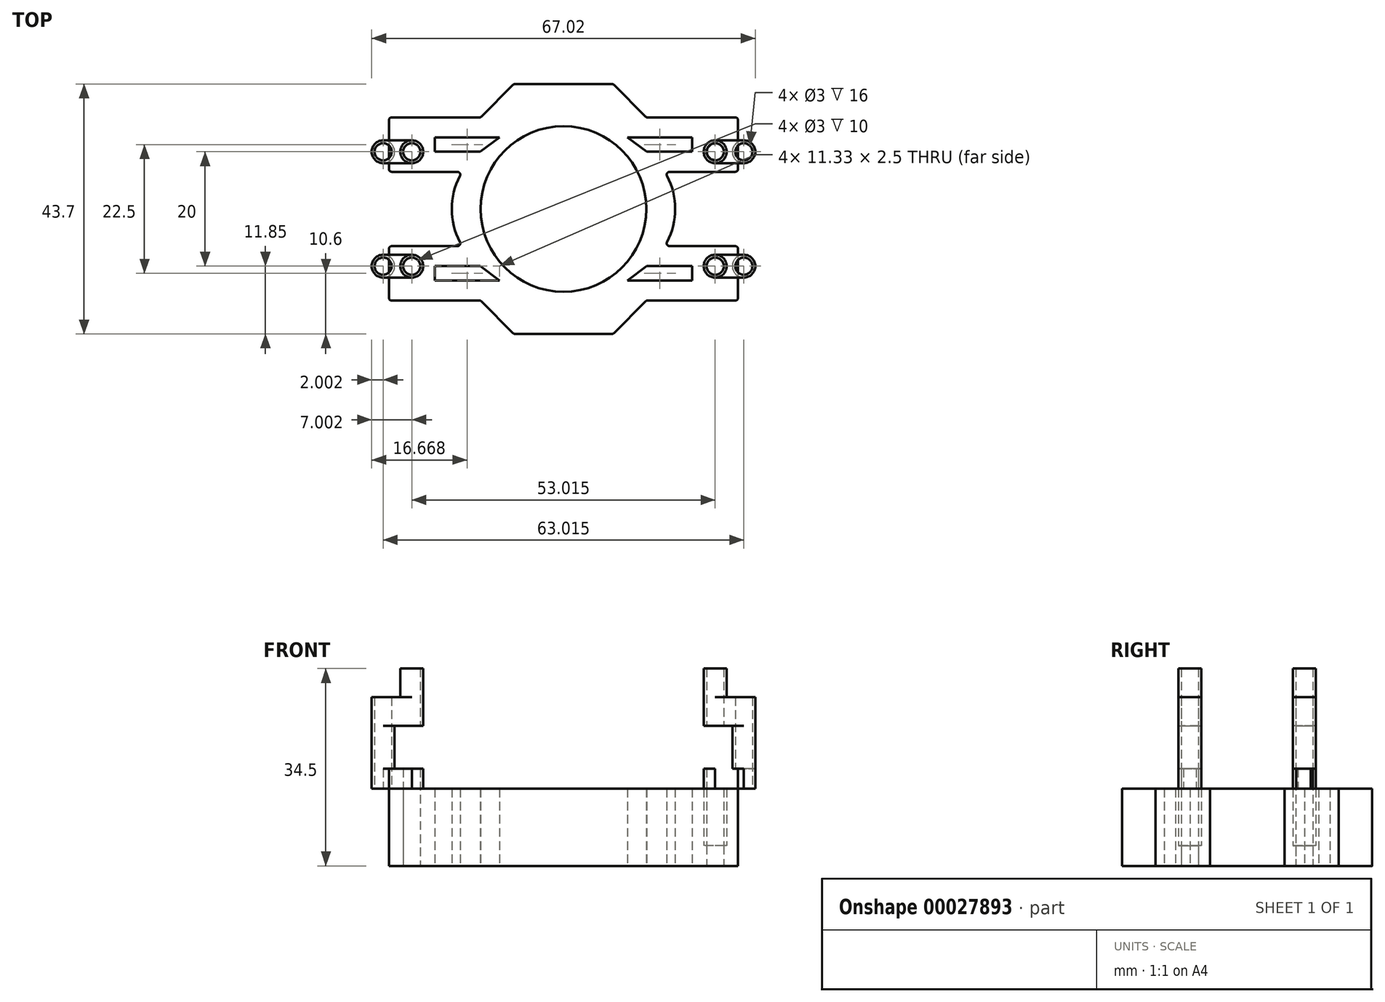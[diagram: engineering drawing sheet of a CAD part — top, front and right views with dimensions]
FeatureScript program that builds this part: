
annotation { "Feature Type Name" : "Feature", "Feature Type Description" : "" }
export const myFeature = defineFeature(function(context is Context, id is Id, definition is map)
    precondition{}
    {
        {
            var Q0;
            Q0=qCreatedBy(makeId("Top.planeOp"),FACE);
            var sketch = newSketch(context, id + "F0", { "sketchPlane" : qUnion([Q0])});
            skLineSegment(sketch, "E0.rect.bottom", {"start": v(30.5, 16) * mm, "end": v(-30.5, 16) * mm});
            skLineSegment(sketch, "E0.rect.top", {"start": v(30.5, -16) * mm, "end": v(-30.5, -16) * mm});
            skLineSegment(sketch, "E0.rect.left", {"start": v(30.5, 16) * mm, "end": v(30.5, -16) * mm});
            skLineSegment(sketch, "E0.rect.right", {"start": v(-30.5, 16) * mm, "end": v(-30.5, -16) * mm});
            skPoint(sketch, "E0.rect.middle", {"position": v(0, 0) * mm});
            skCircle(sketch, "E1", {"center": v(0, 0) * mm, "radius": 14.47 * mm});
            skLineSegment(sketch, "E2.rect.bottom", {"start": v(-19.5, -10) * mm, "end": v(-22.5, -10) * mm});
            skLineSegment(sketch, "E2.rect.top", {"start": v(-19.5, 10) * mm, "end": v(-22.5, 10) * mm});
            skLineSegment(sketch, "E2.rect.left", {"start": v(-19.5, -10) * mm, "end": v(-19.5, 10) * mm});
            skLineSegment(sketch, "E2.rect.right", {"start": v(-22.5, -10) * mm, "end": v(-22.5, 10) * mm});
            skPoint(sketch, "E2.rect.middle", {"position": v(-21, 0) * mm});
            skLineSegment(sketch, "E3.MirrorCS", {"start": v(19.5, 10) * mm, "end": v(22.5, 10) * mm});
            skLineSegment(sketch, "E4.MirrorCS", {"start": v(22.5, -10) * mm, "end": v(22.5, 10) * mm});
            skLineSegment(sketch, "E5.MirrorCS", {"start": v(19.5, -10) * mm, "end": v(22.5, -10) * mm});
            skLineSegment(sketch, "E6.MirrorCS", {"start": v(19.5, -10) * mm, "end": v(19.5, 10) * mm});
            skCircle(sketch, "E7", {"center": v(-26.5, 10) * mm, "radius": 1.5 * mm});
            skCircle(sketch, "E8", {"center": v(-26.5, -10) * mm, "radius": 1.5 * mm});
            skCircle(sketch, "E9.MirrorC", {"center": v(26.5, 10) * mm, "radius": 1.5 * mm});
            skCircle(sketch, "E10.MirrorC", {"center": v(26.5, -10) * mm, "radius": 1.5 * mm});
            skLineSegment(sketch, "E11", {"start": v(-19.5, -10) * mm, "end": v(-14.5, -10) * mm});
            skLineSegment(sketch, "E12", {"start": v(-19.5, 10) * mm, "end": v(-14.5, 10) * mm});
            skArc(sketch, "E13", {"start": v(-14.5, 10) * mm, "mid": v(-19.5, 0) * mm, "end": v(-14.5, -10) * mm});
            skArc(sketch, "E14.MirrorCS", {"start": v(14.5, 10) * mm, "mid": v(19.5, 0) * mm, "end": v(14.5, -10) * mm});
            skLineSegment(sketch, "E15.MirrorCS", {"start": v(19.5, -10) * mm, "end": v(14.5, -10) * mm});
            skLineSegment(sketch, "E16.MirrorCS", {"start": v(19.5, 10) * mm, "end": v(14.5, 10) * mm});
            skLineSegment(sketch, "E17", {"start": v(-22.5, 6.5) * mm, "end": v(-19.5, 6.5) * mm});
            skLineSegment(sketch, "E18", {"start": v(-22.5, -6.5) * mm, "end": v(-19.5, -6.5) * mm});
            skLineSegment(sketch, "E19", {"start": v(-19.5, -6.5) * mm, "end": v(-17.69, -6.5) * mm});
            skLineSegment(sketch, "E20", {"start": v(-19.5, 6.5) * mm, "end": v(-17.69, 6.5) * mm});
            skLineSegment(sketch, "E21.bottom", {"start": v(-22.5, 6.5) * mm, "end": v(-30.5, 6.5) * mm});
            skLineSegment(sketch, "E21.top", {"start": v(-22.5, -6.5) * mm, "end": v(-30.5, -6.5) * mm});
            skLineSegment(sketch, "E21.left", {"start": v(-22.5, 6.5) * mm, "end": v(-22.5, -6.5) * mm});
            skLineSegment(sketch, "E21.right", {"start": v(-30.5, 6.5) * mm, "end": v(-30.5, -6.5) * mm});
            skLineSegment(sketch, "E22.MirrorCS", {"start": v(19.5, 6.5) * mm, "end": v(17.69, 6.5) * mm});
            skLineSegment(sketch, "E23.MirrorCS", {"start": v(22.5, 6.5) * mm, "end": v(19.5, 6.5) * mm});
            skLineSegment(sketch, "E24.MirrorCS", {"start": v(22.5, 6.5) * mm, "end": v(30.5, 6.5) * mm});
            skLineSegment(sketch, "E25.MirrorCS", {"start": v(22.5, -6.5) * mm, "end": v(30.5, -6.5) * mm});
            skLineSegment(sketch, "E26.MirrorCS", {"start": v(22.5, -6.5) * mm, "end": v(19.5, -6.5) * mm});
            skLineSegment(sketch, "E27.MirrorCS", {"start": v(19.5, -6.5) * mm, "end": v(17.69, -6.5) * mm});
            skLineSegment(sketch, "E28", {"start": v(-14.5, -16) * mm, "end": v(-8.66, -21.85) * mm});
            skLineSegment(sketch, "E29", {"start": v(-8.66, -21.85) * mm, "end": v(8.66, -21.85) * mm});
            skLineSegment(sketch, "E30", {"start": v(8.66, -21.85) * mm, "end": v(14.5, -16) * mm});
            skLineSegment(sketch, "E31.MirrorCS", {"start": v(-8.66, -21.85) * mm, "end": v(-8.66, -39.17) * mm});
            skLineSegment(sketch, "E32.MirrorCS", {"start": v(-14.5, 16) * mm, "end": v(-8.66, 21.85) * mm});
            skLineSegment(sketch, "E33.MirrorCS", {"start": v(-8.66, 21.85) * mm, "end": v(8.66, 21.85) * mm});
            skLineSegment(sketch, "E34.MirrorCS", {"start": v(8.66, 21.85) * mm, "end": v(14.5, 16) * mm});
            skLineSegment(sketch, "E35.bottom", {"start": v(-14.5, -10) * mm, "end": v(-22.5, -10) * mm});
            skLineSegment(sketch, "E35.top", {"start": v(-14.5, -12.5) * mm, "end": v(-22.5, -12.5) * mm});
            skLineSegment(sketch, "E35.left", {"start": v(-14.5, -10) * mm, "end": v(-14.5, -12.5) * mm});
            skLineSegment(sketch, "E35.right", {"start": v(-22.5, -10) * mm, "end": v(-22.5, -12.5) * mm});
            skLineSegment(sketch, "E36", {"start": v(30.5, 0) * mm, "end": v(-30.5, 0) * mm, "construction": true});
            skLineSegment(sketch, "E37", {"start": v(0, -21.85) * mm, "end": v(0, 21.85) * mm, "construction": true});
            skLineSegment(sketch, "E38.MirrorCS", {"start": v(-14.5, 12.5) * mm, "end": v(-22.5, 12.5) * mm});
            skLineSegment(sketch, "E39.MirrorCS", {"start": v(-22.5, 10) * mm, "end": v(-22.5, 12.5) * mm});
            skLineSegment(sketch, "E40.MirrorCS", {"start": v(-14.5, 10) * mm, "end": v(-14.5, 12.5) * mm});
            skLineSegment(sketch, "E41.MirrorCS", {"start": v(-45.02, -21.85) * mm, "end": v(-45.02, 21.85) * mm});
            skLineSegment(sketch, "E42.MirrorCS", {"start": v(14.5, 10) * mm, "end": v(14.5, 12.5) * mm});
            skLineSegment(sketch, "E43.MirrorCS", {"start": v(14.5, 12.5) * mm, "end": v(22.5, 12.5) * mm});
            skLineSegment(sketch, "E44.MirrorCS", {"start": v(22.5, 10) * mm, "end": v(22.5, 12.5) * mm});
            skLineSegment(sketch, "E45.MirrorCS", {"start": v(22.5, -10) * mm, "end": v(22.5, -12.5) * mm});
            skLineSegment(sketch, "E46.MirrorCS", {"start": v(14.5, -12.5) * mm, "end": v(22.5, -12.5) * mm});
            skLineSegment(sketch, "E47.MirrorCS", {"start": v(14.5, -10) * mm, "end": v(14.5, -12.5) * mm});
            skLineSegment(sketch, "E48", {"start": v(-14.5, -12.5) * mm, "end": v(-12, -12.5) * mm});
            skLineSegment(sketch, "E49", {"start": v(-14.5, -10) * mm, "end": v(-11.18, -12.5) * mm});
            skLineSegment(sketch, "E50", {"start": v(-11.18, -12.5) * mm, "end": v(-12, -12.5) * mm});
            skLineSegment(sketch, "E51.MirrorCS", {"start": v(14.5, -12.5) * mm, "end": v(12, -12.5) * mm});
            skLineSegment(sketch, "E52.MirrorCS", {"start": v(11.18, -12.5) * mm, "end": v(12, -12.5) * mm});
            skLineSegment(sketch, "E53.MirrorCS", {"start": v(14.5, -10) * mm, "end": v(11.18, -12.5) * mm});
            skLineSegment(sketch, "E54.MirrorCS", {"start": v(14.5, 12.5) * mm, "end": v(12, 12.5) * mm});
            skLineSegment(sketch, "E55.MirrorCS", {"start": v(11.18, 12.5) * mm, "end": v(12, 12.5) * mm});
            skLineSegment(sketch, "E56.MirrorCS", {"start": v(14.5, 10) * mm, "end": v(11.18, 12.5) * mm});
            skLineSegment(sketch, "E57.MirrorCS", {"start": v(-14.5, 12.5) * mm, "end": v(-12, 12.5) * mm});
            skLineSegment(sketch, "E58.MirrorCS", {"start": v(-11.18, 12.5) * mm, "end": v(-12, 12.5) * mm});
            skLineSegment(sketch, "E59.MirrorCS", {"start": v(-14.5, 10) * mm, "end": v(-11.18, 12.5) * mm});
            skSolve(sketch);
        }
        {
            var Q0;
            Q0=makeQuery(id+"F0.imprint","IMPRINT",FACE,{"disambiguationData":[TD([[makeQuery(id+"F0.imprint","IMPRINT",EDGE,{"derivedFrom":sQuery(id+"F0.wireOp",EDGE,"E0.rect.bottom")}),1.0]])]});
            var Q1;
            {var subQ2=sQuery(id+"F0.wireOp",EDGE,"E2.rect.top");Q1=makeQuery(id+"F0.imprint","IMPRINT",FACE,{"disambiguationData":[TD([[makeQuery(id+"F0.imprint","IMPRINT",EDGE,{"derivedFrom":subQ2}),1.0]])]});}
            var Q2;
            {var subQ2=sQuery(id+"F0.wireOp",EDGE,"E12");Q2=makeQuery(id+"F0.imprint","IMPRINT",FACE,{"disambiguationData":[TD([[makeQuery(id+"F0.imprint","IMPRINT",EDGE,{"derivedFrom":subQ2}),-1.0]])]});}
            var Q3;
            {var subQ2=sQuery(id+"F0.wireOp",EDGE,"E2.rect.bottom");Q3=makeQuery(id+"F0.imprint","IMPRINT",FACE,{"disambiguationData":[TD([[makeQuery(id+"F0.imprint","IMPRINT",EDGE,{"derivedFrom":subQ2}),-1.0]])]});}
            var Q4;
            {var subQ2=sQuery(id+"F0.wireOp",EDGE,"E11");Q4=makeQuery(id+"F0.imprint","IMPRINT",FACE,{"disambiguationData":[TD([[makeQuery(id+"F0.imprint","IMPRINT",EDGE,{"derivedFrom":subQ2}),1.0]])]});}
            var Q5;
            {var subQ2=sQuery(id+"F0.wireOp",EDGE,"E16.MirrorCS");Q5=makeQuery(id+"F0.imprint","IMPRINT",FACE,{"disambiguationData":[TD([[makeQuery(id+"F0.imprint","IMPRINT",EDGE,{"derivedFrom":subQ2}),1.0]])]});}
            var Q6;
            {var subQ2=sQuery(id+"F0.wireOp",EDGE,"E3.MirrorCS");Q6=makeQuery(id+"F0.imprint","IMPRINT",FACE,{"disambiguationData":[TD([[makeQuery(id+"F0.imprint","IMPRINT",EDGE,{"derivedFrom":subQ2}),-1.0]])]});}
            var Q7;
            {var subQ1=sQuery(id+"F0.wireOp",EDGE,"E15.MirrorCS");Q7=makeQuery(id+"F0.imprint","IMPRINT",FACE,{"disambiguationData":[TD([[makeQuery(id+"F0.imprint","IMPRINT",EDGE,{"derivedFrom":subQ1}),-1.0]])]});}
            var Q8;
            {var subQ2=sQuery(id+"F0.wireOp",EDGE,"E5.MirrorCS");Q8=makeQuery(id+"F0.imprint","IMPRINT",FACE,{"disambiguationData":[TD([[makeQuery(id+"F0.imprint","IMPRINT",EDGE,{"derivedFrom":subQ2}),1.0]])]});}
            var Q9;
            {var subQ1=sQuery(id+"F0.wireOp",EDGE,"E28");Q9=makeQuery(id+"F0.imprint","IMPRINT",FACE,{"disambiguationData":[TD([[makeQuery(id+"F0.imprint","IMPRINT",EDGE,{"derivedFrom":subQ1}),1.0]])]});}
            var Q10;
            {var subQ1=sQuery(id+"F0.wireOp",EDGE,"E32.MirrorCS");Q10=makeQuery(id+"F0.imprint","IMPRINT",FACE,{"disambiguationData":[TD([[makeQuery(id+"F0.imprint","IMPRINT",EDGE,{"derivedFrom":subQ1}),-1.0]])]});}
            var Q11;
            {var subQ5=sQuery(id+"F0.wireOp",EDGE,"E18");Q11=makeQuery(id+"F0.imprint","IMPRINT",FACE,{"disambiguationData":[TD([[makeQuery(id+"F0.imprint","IMPRINT",EDGE,{"derivedFrom":subQ5}),-1.0]])]});}
            var Q12;
            {var subQ5=sQuery(id+"F0.wireOp",EDGE,"E19");Q12=makeQuery(id+"F0.imprint","IMPRINT",FACE,{"disambiguationData":[TD([[makeQuery(id+"F0.imprint","IMPRINT",EDGE,{"derivedFrom":subQ5}),-1.0]])]});}
            extrude(context, id + "F1", {"entities" : qUnion([Q0, Q1, Q2, Q3, Q4, Q5, Q6, Q7, Q8, Q9, Q10, Q11, Q12]), "depth" : 3.5 * mm});
        }
        {
            var Q0;
            Q0=makeQuery(id+"F1.opExtrude","CAP_FACE",FACE,{"disambiguationData":[OSD([sQuery(id+"F0.wireOp",EDGE,"E0.rect.bottom"),sQuery(id+"F0.wireOp",EDGE,"E0.rect.top"),sQuery(id+"F0.wireOp",EDGE,"E0.rect.left"),sQuery(id+"F0.wireOp",EDGE,"E0.rect.right"),sQuery(id+"F0.wireOp",EDGE,"E1"),sQuery(id+"F0.wireOp",EDGE,"E7"),sQuery(id+"F0.wireOp",EDGE,"E8"),sQuery(id+"F0.wireOp",EDGE,"E9.MirrorC"),sQuery(id+"F0.wireOp",EDGE,"E10.MirrorC"),sQuery(id+"F0.wireOp",EDGE,"E13"),sQuery(id+"F0.wireOp",EDGE,"E14.MirrorCS"),sQuery(id+"F0.wireOp",EDGE,"E17"),sQuery(id+"F0.wireOp",EDGE,"E18"),sQuery(id+"F0.wireOp",EDGE,"E19"),sQuery(id+"F0.wireOp",EDGE,"E21.bottom"),sQuery(id+"F0.wireOp",EDGE,"E21.top"),sQuery(id+"F0.wireOp",EDGE,"E20"),sQuery(id+"F0.wireOp",EDGE,"E22.MirrorCS"),sQuery(id+"F0.wireOp",EDGE,"E23.MirrorCS"),sQuery(id+"F0.wireOp",EDGE,"E24.MirrorCS"),sQuery(id+"F0.wireOp",EDGE,"E25.MirrorCS"),sQuery(id+"F0.wireOp",EDGE,"E26.MirrorCS"),sQuery(id+"F0.wireOp",EDGE,"E27.MirrorCS")])],"isStart":false});
            var sketch = newSketch(context, id + "F2", { "sketchPlane" : qUnion([Q0])});
            skCircle(sketch, "E60", {"center": v(-26.5, 10) * mm, "radius": 1.5 * mm});
            skCircle(sketch, "E61", {"center": v(-26.5, 10) * mm, "radius": 2 * mm});
            skCircle(sketch, "E62.MirrorC", {"center": v(26.5, 10) * mm, "radius": 2 * mm});
            skCircle(sketch, "E63.MirrorC", {"center": v(26.5, 10) * mm, "radius": 1.5 * mm});
            skCircle(sketch, "E64.MirrorC", {"center": v(-26.5, -10) * mm, "radius": 1.5 * mm});
            skCircle(sketch, "E65.MirrorC", {"center": v(-26.5, -10) * mm, "radius": 2 * mm});
            skCircle(sketch, "E66.MirrorC", {"center": v(26.5, -10) * mm, "radius": 1.5 * mm});
            skCircle(sketch, "E67.MirrorC", {"center": v(26.5, -10) * mm, "radius": 2 * mm});
            skSolve(sketch);
        }
        {
            var Q0;
            Q0=makeQuery(id+"F2.imprint","IMPRINT",FACE,{"disambiguationData":[TD([[makeQuery(id+"F2.imprint","IMPRINT",EDGE,{"derivedFrom":sQuery(id+"F2.wireOp",EDGE,"E60")}),-1.0]])]});
            var Q1;
            Q1=makeQuery(id+"F2.imprint","IMPRINT",FACE,{"disambiguationData":[TD([[makeQuery(id+"F2.imprint","IMPRINT",EDGE,{"derivedFrom":sQuery(id+"F2.wireOp",EDGE,"E64.MirrorC")}),-1.0]])]});
            var Q2;
            Q2=makeQuery(id+"F2.imprint","IMPRINT",FACE,{"disambiguationData":[TD([[makeQuery(id+"F2.imprint","IMPRINT",EDGE,{"derivedFrom":sQuery(id+"F2.wireOp",EDGE,"E66.MirrorC")}),1.0]])]});
            var Q3;
            Q3=makeQuery(id+"F2.imprint","IMPRINT",FACE,{"disambiguationData":[TD([[makeQuery(id+"F2.imprint","IMPRINT",EDGE,{"derivedFrom":sQuery(id+"F2.wireOp",EDGE,"E62.MirrorC")}),-1.0]])]});
            extrude(context, id + "F3", {"entities" : qUnion([Q0, Q1, Q2, Q3]), "operationType" : NewBodyOperationType.ADD, "depth" : 10 * mm});
        }
        {
            var Q0;
            Q0=makeQuery(id+"F1.opExtrude","SWEPT_EDGE",EDGE,{"disambiguationData":[OSD([sQuery(id+"F0.wireOp",EDGE,"E14.MirrorCS"),sQuery(id+"F0.wireOp",EDGE,"E22.MirrorCS")])]});
            var Q1;
            Q1=makeQuery(id+"F1.opExtrude","SWEPT_EDGE",EDGE,{"disambiguationData":[OSD([sQuery(id+"F0.wireOp",EDGE,"E14.MirrorCS"),sQuery(id+"F0.wireOp",EDGE,"E27.MirrorCS")])]});
            var Q2;
            Q2=makeQuery(id+"F1.opExtrude","SWEPT_EDGE",EDGE,{"disambiguationData":[OSD([sQuery(id+"F0.wireOp",EDGE,"E13"),sQuery(id+"F0.wireOp",EDGE,"E20")])]});
            var Q3;
            Q3=makeQuery(id+"F1.opExtrude","SWEPT_EDGE",EDGE,{"disambiguationData":[OSD([sQuery(id+"F0.wireOp",EDGE,"E13"),sQuery(id+"F0.wireOp",EDGE,"E19")])]});
            var Q4;
            Q4=makeQuery(id+"F1.opExtrude","SWEPT_EDGE",EDGE,{"disambiguationData":[OSD([sQuery(id+"F0.wireOp",EDGE,"E0.rect.top"),sQuery(id+"F0.wireOp",EDGE,"E0.rect.right")])]});
            var Q5;
            Q5=makeQuery(id+"F1.opExtrude","SWEPT_EDGE",EDGE,{"disambiguationData":[OSD([sQuery(id+"F0.wireOp",EDGE,"E0.rect.top"),sQuery(id+"F0.wireOp",EDGE,"E0.rect.left")])]});
            var Q6;
            Q6=makeQuery(id+"F1.opExtrude","SWEPT_EDGE",EDGE,{"disambiguationData":[OSD([sQuery(id+"F0.wireOp",EDGE,"E0.rect.left"),sQuery(id+"F0.wireOp",EDGE,"E25.MirrorCS")])]});
            var Q7;
            Q7=makeQuery(id+"F1.opExtrude","SWEPT_EDGE",EDGE,{"disambiguationData":[OSD([sQuery(id+"F0.wireOp",EDGE,"E0.rect.bottom"),sQuery(id+"F0.wireOp",EDGE,"E0.rect.left")])]});
            var Q8;
            Q8=makeQuery(id+"F1.opExtrude","SWEPT_EDGE",EDGE,{"disambiguationData":[OSD([sQuery(id+"F0.wireOp",EDGE,"E0.rect.left"),sQuery(id+"F0.wireOp",EDGE,"E24.MirrorCS")])]});
            var Q9;
            Q9=makeQuery(id+"F1.opExtrude","SWEPT_EDGE",EDGE,{"disambiguationData":[OSD([sQuery(id+"F0.wireOp",EDGE,"E0.rect.right"),sQuery(id+"F0.wireOp",EDGE,"E21.bottom"),sQuery(id+"F0.wireOp",EDGE,"E21.right")])]});
            var Q10;
            Q10=makeQuery(id+"F1.opExtrude","SWEPT_EDGE",EDGE,{"disambiguationData":[OSD([sQuery(id+"F0.wireOp",EDGE,"E0.rect.bottom"),sQuery(id+"F0.wireOp",EDGE,"E0.rect.right")])]});
            var Q11;
            Q11=makeQuery(id+"F1.opExtrude","SWEPT_EDGE",EDGE,{"disambiguationData":[OSD([sQuery(id+"F0.wireOp",EDGE,"E0.rect.right"),sQuery(id+"F0.wireOp",EDGE,"E21.top"),sQuery(id+"F0.wireOp",EDGE,"E21.right")])]});
            fillet(context, id + "F4", {"entities" : qUnion([Q0, Q1, Q2, Q3, Q4, Q5, Q6, Q7, Q8, Q9, Q10, Q11]), "radius" : .5 * mm, "tangentPropagation" : true, "allowEdgeOverflow" : false});
        }
        {
            var Q0;
            Q0=makeQuery(id+"F3.opExtrude","CAP_FACE",FACE,{"disambiguationData":[OSD([sQuery(id+"F2.wireOp",EDGE,"E60"),sQuery(id+"F2.wireOp",EDGE,"E61")])],"isStart":false});
            var sketch = newSketch(context, id + "F5", { "sketchPlane" : qUnion([Q0])});
            skLineSegment(sketch, "E68", {"start": v(-26.5, 12) * mm, "end": v(-26.5, 8) * mm, "construction": true});
            skLineSegment(sketch, "E69.bottom", {"start": v(-26.5, 12) * mm, "end": v(-31.5, 12) * mm});
            skLineSegment(sketch, "E69.top", {"start": v(-26.5, 8) * mm, "end": v(-31.5, 8) * mm});
            skLineSegment(sketch, "E69.right", {"start": v(-31.5, 12) * mm, "end": v(-31.5, 8) * mm});
            skArc(sketch, "E70", {"start": v(-31.5, 12) * mm, "mid": v(-33.5, 10) * mm, "end": v(-31.5, 8) * mm});
            skCircle(sketch, "E71", {"center": v(-31.5, 10) * mm, "radius": 1.5 * mm});
            skLineSegment(sketch, "E72", {"start": v(0, 59.27) * mm, "end": v(0, -61.45) * mm, "construction": true});
            skLineSegment(sketch, "E73", {"start": v(-74.65, 0) * mm, "end": v(75.38, 0) * mm, "construction": true});
            skLineSegment(sketch, "E74.MirrorCS", {"start": v(26.5, 12) * mm, "end": v(31.5, 12) * mm});
            skLineSegment(sketch, "E75.MirrorCS", {"start": v(26.5, 12) * mm, "end": v(26.5, 8) * mm});
            skLineSegment(sketch, "E76.MirrorCS", {"start": v(26.5, 8) * mm, "end": v(31.5, 8) * mm});
            skArc(sketch, "E77.MirrorCS", {"start": v(31.5, 12) * mm, "mid": v(33.5, 10) * mm, "end": v(31.5, 8) * mm});
            skCircle(sketch, "E78.MirrorC", {"center": v(31.5, 10) * mm, "radius": 1.5 * mm});
            skLineSegment(sketch, "E79.MirrorCS", {"start": v(31.5, 12) * mm, "end": v(31.5, 8) * mm});
            skLineSegment(sketch, "E80.MirrorCS", {"start": v(-26.5, -8) * mm, "end": v(-31.5, -8) * mm});
            skLineSegment(sketch, "E81.MirrorCS", {"start": v(-26.5, -12) * mm, "end": v(-26.5, -8) * mm});
            skLineSegment(sketch, "E82.MirrorCS", {"start": v(-26.5, -12) * mm, "end": v(-31.5, -12) * mm});
            skArc(sketch, "E83.MirrorCS", {"start": v(-31.5, -12) * mm, "mid": v(-33.5, -10) * mm, "end": v(-31.5, -8) * mm});
            skLineSegment(sketch, "E84.MirrorCS", {"start": v(-31.5, -12) * mm, "end": v(-31.5, -8) * mm, "construction": true});
            skCircle(sketch, "E85.MirrorC", {"center": v(-31.5, -10) * mm, "radius": 1.5 * mm});
            skLineSegment(sketch, "E86.MirrorCS", {"start": v(-26.5, 12) * mm, "end": v(-26.5, 8) * mm});
            skLineSegment(sketch, "E87.MirrorCS", {"start": v(26.5, -8) * mm, "end": v(31.5, -8) * mm});
            skLineSegment(sketch, "E88.MirrorCS", {"start": v(26.5, -12) * mm, "end": v(26.5, -8) * mm});
            skLineSegment(sketch, "E89.MirrorCS", {"start": v(26.5, -12) * mm, "end": v(31.5, -12) * mm});
            skLineSegment(sketch, "E90.MirrorCS", {"start": v(31.5, -12) * mm, "end": v(31.5, -8) * mm});
            skCircle(sketch, "E91.MirrorC", {"center": v(31.5, -10) * mm, "radius": 1.5 * mm});
            skArc(sketch, "E92.MirrorCS", {"start": v(31.5, -12) * mm, "mid": v(33.5, -10) * mm, "end": v(31.5, -8) * mm});
            skArc(sketch, "E93", {"start": v(-26.5, 8) * mm, "mid": v(-24.5, 10) * mm, "end": v(-26.5, 12) * mm});
            skArc(sketch, "E94.MirrorCS", {"start": v(-26.5, -8) * mm, "mid": v(-24.5, -10) * mm, "end": v(-26.5, -12) * mm});
            skArc(sketch, "E95.MirrorCS", {"start": v(26.5, -8) * mm, "mid": v(24.5, -10) * mm, "end": v(26.5, -12) * mm});
            skArc(sketch, "E96.MirrorCS", {"start": v(26.5, 8) * mm, "mid": v(24.5, 10) * mm, "end": v(26.5, 12) * mm});
            skArc(sketch, "E97.MirrorCS", {"start": v(26.5, 8) * mm, "mid": v(28.5, 10) * mm, "end": v(26.5, 12) * mm});
            skCircle(sketch, "E98", {"center": v(26.5, 10) * mm, "radius": 1.46 * mm});
            skCircle(sketch, "E99", {"center": v(26.5, -10) * mm, "radius": 1.5 * mm});
            skCircle(sketch, "E100", {"center": v(-26.5, -10) * mm, "radius": 1.5 * mm});
            skSolve(sketch);
        }
        {
            var Q0;
            Q0=makeQuery(id+"F5.imprint","IMPRINT",FACE,{"disambiguationData":[TD([[makeQuery(id+"F5.imprint","IMPRINT",EDGE,{"derivedFrom":sQuery(id+"F5.wireOp",EDGE,"E75.MirrorCS")}),-1.0]])]});
            var Q1;
            Q1=makeQuery(id+"F5.imprint","IMPRINT",FACE,{"disambiguationData":[TD([[makeQuery(id+"F5.imprint","IMPRINT",EDGE,{"derivedFrom":sQuery(id+"F5.wireOp",EDGE,"E81.MirrorCS")}),-1.0]])]});
            var Q2;
            Q2=makeQuery(id+"F5.imprint","IMPRINT",FACE,{"disambiguationData":[TD([[makeQuery(id+"F5.imprint","IMPRINT",EDGE,{"derivedFrom":sQuery(id+"F5.wireOp",EDGE,"E88.MirrorCS")}),1.0]])]});
            var Q3;
            {var subQ0=sQuery(id+"F5.wireOp",EDGE,"E70");Q3=makeQuery(id+"F5.imprint","IMPRINT",FACE,{"disambiguationData":[TD([[makeQuery(id+"F5.imprint","IMPRINT",EDGE,{"derivedFrom":subQ0}),1.0]])]});}
            var Q4;
            {var subQ3=sQuery(id+"F5.wireOp",EDGE,"E77.MirrorCS");Q4=makeQuery(id+"F5.imprint","IMPRINT",FACE,{"disambiguationData":[TD([[makeQuery(id+"F5.imprint","IMPRINT",EDGE,{"derivedFrom":subQ3}),-1.0]])]});}
            var Q5;
            Q5=makeQuery(id+"F5.imprint","IMPRINT",FACE,{"disambiguationData":[TD([[makeQuery(id+"F5.imprint","IMPRINT",EDGE,{"derivedFrom":sQuery(id+"F5.wireOp",EDGE,"E80.MirrorCS")}),1.0]])]});
            var Q6;
            {var subQ0=sQuery(id+"F5.wireOp",EDGE,"E92.MirrorCS");Q6=makeQuery(id+"F5.imprint","IMPRINT",FACE,{"disambiguationData":[TD([[makeQuery(id+"F5.imprint","IMPRINT",EDGE,{"derivedFrom":subQ0}),1.0]])]});}
            var Q7;
            {var subQ4=sQuery(id+"F5.wireOp",EDGE,"E69.bottom");Q7=makeQuery(id+"F5.imprint","IMPRINT",FACE,{"disambiguationData":[TD([[makeQuery(id+"F5.imprint","IMPRINT",EDGE,{"derivedFrom":subQ4}),1.0]])]});}
            var Q8;
            {var subQ3=sQuery(id+"F5.wireOp",EDGE,"E74.MirrorCS");Q8=makeQuery(id+"F5.imprint","IMPRINT",FACE,{"disambiguationData":[TD([[makeQuery(id+"F5.imprint","IMPRINT",EDGE,{"derivedFrom":subQ3}),-1.0]])]});}
            var Q9;
            {var subQ4=sQuery(id+"F5.wireOp",EDGE,"E87.MirrorCS");Q9=makeQuery(id+"F5.imprint","IMPRINT",FACE,{"disambiguationData":[TD([[makeQuery(id+"F5.imprint","IMPRINT",EDGE,{"derivedFrom":subQ4}),-1.0]])]});}
            var Q10;
            {var subQ4=sQuery(id+"F5.wireOp",EDGE,"E93");Q10=makeQuery(id+"F5.imprint","IMPRINT",FACE,{"disambiguationData":[TD([[makeQuery(id+"F5.imprint","IMPRINT",EDGE,{"derivedFrom":subQ4}),1.0]])]});}
            var Q11;
            {var subQ0=makeQuery(id+"F3.opExtrude","CAP_EDGE",EDGE,{"disambiguationData":[OSD([sQuery(id+"F2.wireOp",EDGE,"E60")])],"isStart":false});var subQ1=sQuery(id+"F5.wireOp",EDGE,"E86.MirrorCS");var subQ3=makeQuery(id+"F5.imprint","INTERSECT",VERTEX,{"disambiguationData":[OD(0.0)],"derivedFrom":[subQ0,subQ1]});Q11=makeQuery(id+"F5.imprint","IMPRINT",FACE,{"disambiguationData":[TD([[makeQuery(id+"F5.imprint","IMPRINT",EDGE,{"disambiguationData":[TD([[subQ3,-1.0]])],"derivedFrom":subQ0}),-1.0]])]});}
            extrude(context, id + "F6", {"entities" : qUnion([Q0, Q1, Q2, Q3, Q4, Q5, Q6, Q7, Q8, Q9, Q10, Q11]), "operationType" : NewBodyOperationType.ADD, "depth" : 3.5 * mm});
        }
        {
            var Q0;
            Q0=makeQuery(id+"F6.opExtrude","CAP_FACE",FACE,{"disambiguationData":[OSD([sQuery(id+"F5.wireOp",EDGE,"E69.bottom"),sQuery(id+"F5.wireOp",EDGE,"E69.top"),sQuery(id+"F5.wireOp",EDGE,"E70"),sQuery(id+"F5.wireOp",EDGE,"E71"),sQuery(id+"F5.wireOp",EDGE,"E93")])],"isStart":false});
            var sketch = newSketch(context, id + "F7", { "sketchPlane" : qUnion([Q0])});
            skCircle(sketch, "E101", {"center": v(-31.5, 10) * mm, "radius": 1.5 * mm});
            skPoint(sketch, "E101.first.point", {"position": v(-32.74, 10.86) * mm});
            skPoint(sketch, "E101.second.point", {"position": v(-31.26, 8.52) * mm});
            skPoint(sketch, "E101.third.point", {"position": v(-30, 9.93) * mm});
            skCircle(sketch, "E102", {"center": v(-31.5, 10) * mm, "radius": 2 * mm});
            skLineSegment(sketch, "E103", {"start": v(-40.42, 0) * mm, "end": v(43.15, 0) * mm, "construction": true});
            skLineSegment(sketch, "E104", {"start": v(0, 39.6) * mm, "end": v(0, -43.6) * mm, "construction": true});
            skCircle(sketch, "E105.MirrorC", {"center": v(-31.5, -10) * mm, "radius": 1.5 * mm});
            skCircle(sketch, "E106.MirrorC", {"center": v(-31.5, -10) * mm, "radius": 2 * mm});
            skCircle(sketch, "E107.MirrorC", {"center": v(31.5, 10) * mm, "radius": 1.5 * mm});
            skCircle(sketch, "E108.MirrorC", {"center": v(31.5, 10) * mm, "radius": 2 * mm});
            skCircle(sketch, "E109.MirrorC", {"center": v(31.5, -10) * mm, "radius": 1.5 * mm});
            skCircle(sketch, "E110.MirrorC", {"center": v(31.5, -10) * mm, "radius": 2 * mm});
            skSolve(sketch);
        }
        {
            var Q0;
            Q0 = qSketchRegion(id + "F7", true);
            extrude(context, id + "F8", {"entities" : qUnion([Q0]), "operationType" : NewBodyOperationType.ADD, "depth" : 7.5 * mm});
        }
        {
            var Q0;
            Q0=makeQuery(id+"F8.opExtrude","CAP_FACE",FACE,{"disambiguationData":[OSD([sQuery(id+"F7.wireOp",EDGE,"E107.MirrorC"),sQuery(id+"F7.wireOp",EDGE,"E108.MirrorC")])],"isStart":false});
            var sketch = newSketch(context, id + "F9", { "sketchPlane" : qUnion([Q0])});
            skLineSegment(sketch, "E111", {"start": v(31.5, 12) * mm, "end": v(31.5, 8) * mm, "construction": true});
            skCircle(sketch, "E112", {"center": v(31.5, 10) * mm, "radius": 2 * mm});
            skLineSegment(sketch, "E113.bottom", {"start": v(31.5, 12) * mm, "end": v(26.5, 12) * mm});
            skLineSegment(sketch, "E113.top", {"start": v(31.5, 8) * mm, "end": v(26.5, 8) * mm});
            skLineSegment(sketch, "E113.left", {"start": v(31.5, 12) * mm, "end": v(31.5, 8) * mm});
            skLineSegment(sketch, "E113.right", {"start": v(26.5, 12) * mm, "end": v(26.5, 8) * mm});
            skCircle(sketch, "E114", {"center": v(26.5, 10) * mm, "radius": 2 * mm});
            skCircle(sketch, "E115", {"center": v(26.5, 10) * mm, "radius": 1.5 * mm});
            skLineSegment(sketch, "E116", {"start": v(-34.96, 0) * mm, "end": v(33.92, 0) * mm, "construction": true});
            skLineSegment(sketch, "E117", {"start": v(0, 32.48) * mm, "end": v(0, -29.83) * mm, "construction": true});
            skLineSegment(sketch, "E118.MirrorCS", {"start": v(31.5, -8) * mm, "end": v(26.5, -8) * mm});
            skCircle(sketch, "E119.MirrorC", {"center": v(31.5, -10) * mm, "radius": 2 * mm});
            skLineSegment(sketch, "E120.MirrorCS", {"start": v(31.5, -12) * mm, "end": v(31.5, -8) * mm});
            skLineSegment(sketch, "E121.MirrorCS", {"start": v(31.5, -12) * mm, "end": v(26.5, -12) * mm});
            skCircle(sketch, "E122.MirrorC", {"center": v(26.5, -10) * mm, "radius": 2 * mm});
            skCircle(sketch, "E123.MirrorC", {"center": v(26.5, -10) * mm, "radius": 1.5 * mm});
            skLineSegment(sketch, "E124.MirrorCS", {"start": v(26.5, -12) * mm, "end": v(26.5, -8) * mm});
            skCircle(sketch, "E125.MirrorC", {"center": v(-26.5, 10) * mm, "radius": 1.5 * mm});
            skLineSegment(sketch, "E126.MirrorCS", {"start": v(-26.5, 12) * mm, "end": v(-26.5, 8) * mm});
            skCircle(sketch, "E127.MirrorC", {"center": v(-26.5, 10) * mm, "radius": 2 * mm});
            skLineSegment(sketch, "E128.MirrorCS", {"start": v(-31.5, 8) * mm, "end": v(-26.5, 8) * mm});
            skLineSegment(sketch, "E129.MirrorCS", {"start": v(-31.5, 12) * mm, "end": v(-26.5, 12) * mm});
            skCircle(sketch, "E130.MirrorC", {"center": v(-31.5, 10) * mm, "radius": 2 * mm});
            skLineSegment(sketch, "E131.MirrorCS", {"start": v(-31.5, 12) * mm, "end": v(-31.5, 8) * mm});
            skCircle(sketch, "E132.MirrorC", {"center": v(-26.5, -10) * mm, "radius": 1.5 * mm});
            skCircle(sketch, "E133.MirrorC", {"center": v(-26.5, -10) * mm, "radius": 2 * mm});
            skLineSegment(sketch, "E134.MirrorCS", {"start": v(-31.5, -8) * mm, "end": v(-26.5, -8) * mm});
            skLineSegment(sketch, "E135.MirrorCS", {"start": v(-26.5, -12) * mm, "end": v(-26.5, -8) * mm});
            skLineSegment(sketch, "E136.MirrorCS", {"start": v(-31.5, -12) * mm, "end": v(-26.5, -12) * mm});
            skCircle(sketch, "E137.MirrorC", {"center": v(-31.5, -10) * mm, "radius": 2 * mm});
            skLineSegment(sketch, "E138.MirrorCS", {"start": v(-31.5, -12) * mm, "end": v(-31.5, -8) * mm});
            skCircle(sketch, "E139", {"center": v(-31.5, 10) * mm, "radius": 1.5 * mm});
            skCircle(sketch, "E140", {"center": v(-31.5, -10) * mm, "radius": 1.5 * mm});
            skCircle(sketch, "E141", {"center": v(31.5, -10) * mm, "radius": 1.5 * mm});
            skCircle(sketch, "E142", {"center": v(31.5, 10) * mm, "radius": 1.5 * mm});
            skSolve(sketch);
        }
        {
            var Q0;
            Q0 = qSketchRegion(id + "F9", true);
            extrude(context, id + "F10", {"entities" : qUnion([Q0]), "operationType" : NewBodyOperationType.ADD, "depth" : 5 * mm});
        }
        {
            var Q0;
            Q0=makeQuery(id+"F10.opExtrude","CAP_FACE",FACE,{"disambiguationData":[OSD([sQuery(id+"F9.wireOp",EDGE,"E132.MirrorC"),sQuery(id+"F9.wireOp",EDGE,"E133.MirrorC"),sQuery(id+"F9.wireOp",EDGE,"E134.MirrorCS"),sQuery(id+"F9.wireOp",EDGE,"E136.MirrorCS"),sQuery(id+"F9.wireOp",EDGE,"E137.MirrorC")])],"isStart":false});
            var sketch = newSketch(context, id + "F11", { "sketchPlane" : qUnion([Q0])});
            skLineSegment(sketch, "E143", {"start": v(-26.5, -8) * mm, "end": v(-26.5, -12) * mm, "construction": true});
            skCircle(sketch, "E144", {"center": v(-26.5, -10) * mm, "radius": 1.5 * mm});
            skCircle(sketch, "E145", {"center": v(-26.5, -10) * mm, "radius": 2 * mm});
            skLineSegment(sketch, "E146", {"start": v(-38.43, 0) * mm, "end": v(34.63, 0) * mm, "construction": true});
            skLineSegment(sketch, "E147", {"start": v(0, 22.93) * mm, "end": v(0, -30.78) * mm, "construction": true});
            skCircle(sketch, "E148.MirrorC", {"center": v(-26.5, 10) * mm, "radius": 1.5 * mm});
            skCircle(sketch, "E149.MirrorC", {"center": v(-26.5, 10) * mm, "radius": 2 * mm});
            skCircle(sketch, "E150.MirrorC", {"center": v(26.5, 10) * mm, "radius": 1.5 * mm});
            skCircle(sketch, "E151.MirrorC", {"center": v(26.5, 10) * mm, "radius": 2 * mm});
            skCircle(sketch, "E152.MirrorC", {"center": v(26.5, -10) * mm, "radius": 1.5 * mm});
            skCircle(sketch, "E153.MirrorC", {"center": v(26.5, -10) * mm, "radius": 2 * mm});
            skSolve(sketch);
        }
        {
            var Q0;
            Q0 = qSketchRegion(id + "F11", true);
            extrude(context, id + "F12", {"entities" : qUnion([Q0]), "operationType" : NewBodyOperationType.ADD, "depth" : 5 * mm});
        }
        {
            var Q0;
            Q0=makeQuery(id+"F1.opExtrude","SWEPT_EDGE",EDGE,{"disambiguationData":[OSD([sQuery(id+"F0.wireOp",EDGE,"E29"),sQuery(id+"F0.wireOp",EDGE,"E30")])]});
            var Q1;
            Q1=makeQuery(id+"F1.opExtrude","SWEPT_EDGE",EDGE,{"disambiguationData":[OSD([sQuery(id+"F0.wireOp",EDGE,"E28"),sQuery(id+"F0.wireOp",EDGE,"E29")])]});
            var Q2;
            Q2=makeQuery(id+"F1.opExtrude","SWEPT_EDGE",EDGE,{"disambiguationData":[OSD([sQuery(id+"F0.wireOp",EDGE,"E0.rect.top"),sQuery(id+"F0.wireOp",EDGE,"E30")])]});
            var Q3;
            Q3=makeQuery(id+"F1.opExtrude","SWEPT_EDGE",EDGE,{"disambiguationData":[OSD([sQuery(id+"F0.wireOp",EDGE,"E0.rect.top"),sQuery(id+"F0.wireOp",EDGE,"E28")])]});
            var Q4;
            Q4=makeQuery(id+"F1.opExtrude","SWEPT_EDGE",EDGE,{"disambiguationData":[OSD([sQuery(id+"F0.wireOp",EDGE,"E0.rect.bottom"),sQuery(id+"F0.wireOp",EDGE,"E34.MirrorCS")])]});
            var Q5;
            Q5=makeQuery(id+"F1.opExtrude","SWEPT_EDGE",EDGE,{"disambiguationData":[OSD([sQuery(id+"F0.wireOp",EDGE,"E33.MirrorCS"),sQuery(id+"F0.wireOp",EDGE,"E34.MirrorCS")])]});
            var Q6;
            Q6=makeQuery(id+"F1.opExtrude","SWEPT_EDGE",EDGE,{"disambiguationData":[OSD([sQuery(id+"F0.wireOp",EDGE,"E32.MirrorCS"),sQuery(id+"F0.wireOp",EDGE,"E33.MirrorCS")])]});
            var Q7;
            Q7=makeQuery(id+"F1.opExtrude","SWEPT_EDGE",EDGE,{"disambiguationData":[OSD([sQuery(id+"F0.wireOp",EDGE,"E0.rect.bottom"),sQuery(id+"F0.wireOp",EDGE,"E32.MirrorCS")])]});
            fillet(context, id + "F13", {"entities" : qUnion([Q0, Q1, Q2, Q3, Q4, Q5, Q6, Q7]), "radius" : .5 * mm, "tangentPropagation" : true, "allowEdgeOverflow" : false});
        }
    });
